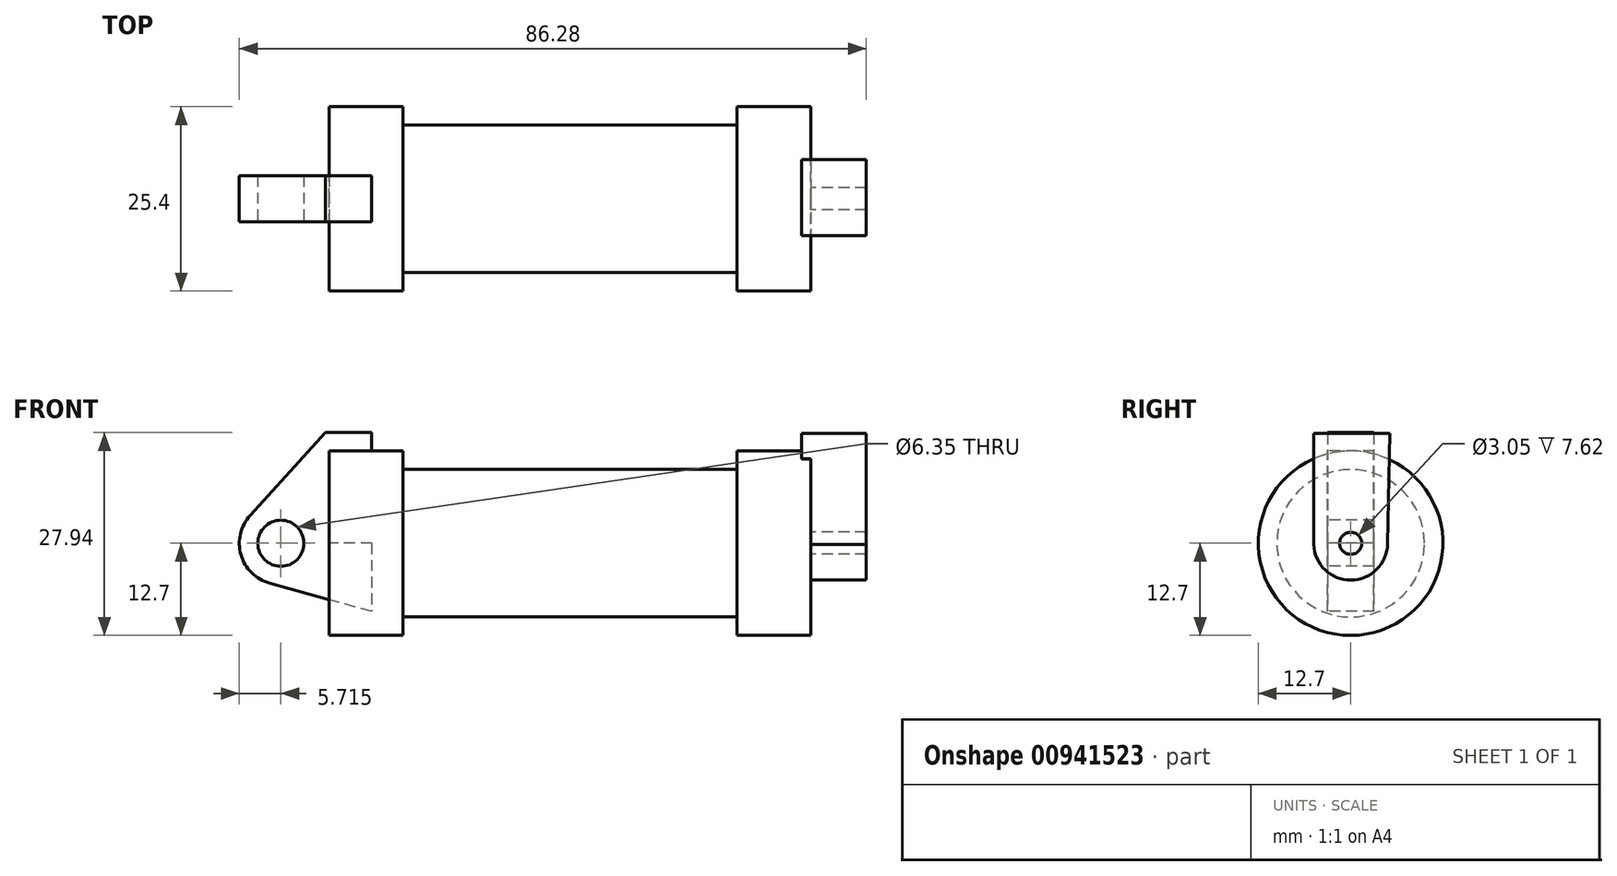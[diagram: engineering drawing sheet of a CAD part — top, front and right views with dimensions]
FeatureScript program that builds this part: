
annotation { "Feature Type Name" : "Feature", "Feature Type Description" : "" }
export const myFeature = defineFeature(function(context is Context, id is Id, definition is map)
    precondition{}
    {
        {
            var Q0;
            Q0=qCreatedBy(makeId("Front.planeOp"),FACE);
            var sketch = newSketch(context, id + "F0", { "sketchPlane" : qUnion([Q0])});
            skLineSegment(sketch, "E0", {"start": v(0, 0) * mm, "end": v(0, 12.7) * mm});
            skLineSegment(sketch, "E1", {"start": v(0, 12.7) * mm, "end": v(10.16, 12.7) * mm});
            skLineSegment(sketch, "E2", {"start": v(10.16, 12.7) * mm, "end": v(10.16, 10.16) * mm});
            skLineSegment(sketch, "E3", {"start": v(10.16, 10.16) * mm, "end": v(56.13, 10.16) * mm});
            skLineSegment(sketch, "E4", {"start": v(56.13, 10.16) * mm, "end": v(56.13, 12.7) * mm});
            skLineSegment(sketch, "E5", {"start": v(56.13, 12.7) * mm, "end": v(66.3, 12.7) * mm});
            skLineSegment(sketch, "E6", {"start": v(66.3, 12.7) * mm, "end": v(66.3, 0) * mm});
            skLineSegment(sketch, "E7", {"start": v(66.3, 0) * mm, "end": v(0, 0) * mm});
            skLineSegment(sketch, "E8", {"start": v(5.84, 15.24) * mm, "end": v(-0.5, 15.24) * mm});
            skLineSegment(sketch, "E9", {"start": v(-0.5, 15.24) * mm, "end": v(-10.88, 3.85) * mm});
            skLineSegment(sketch, "E10", {"start": v(0, 0) * mm, "end": v(-6.65, 0) * mm});
            skCircle(sketch, "E11", {"center": v(-6.65, 0) * mm, "radius": 5.72 * mm});
            skCircle(sketch, "E12", {"center": v(-6.65, 0) * mm, "radius": 3.18 * mm});
            skLineSegment(sketch, "E13", {"start": v(5.84, 15.24) * mm, "end": v(5.84, -9.4) * mm});
            skLineSegment(sketch, "E14", {"start": v(5.84, -9.4) * mm, "end": v(-8.18, -5.5) * mm});
            skSolve(sketch);
        }
        {
            var Q0;
            {var subQ0=sQuery(id+"F0.wireOp",EDGE,"E0");Q0=makeQuery(id+"F0.imprint","IMPRINT",FACE,{"disambiguationData":[TD([[makeQuery(id+"F0.imprint","IMPRINT",EDGE,{"derivedFrom":subQ0}),-1.0]])]});}
            var Q1;
            {var subQ0=sQuery(id+"F0.wireOp",EDGE,"E2");Q1=makeQuery(id+"F0.imprint","IMPRINT",FACE,{"disambiguationData":[TD([[makeQuery(id+"F0.imprint","IMPRINT",EDGE,{"derivedFrom":subQ0}),-1.0]])]});}
            var Q2;
            Q2=sQuery(id+"F0.wireOp",EDGE,"E7");
            revolve(context, id + "F1", {"surfaceOperationType" : NewSurfaceOperationType.NEW, "entities" : qUnion([Q0, Q1]), "axis" : qUnion([Q2]), "revolveType" : RevolveType.FULL});
        }
        {
            var Q0;
            {var subQ1=sQuery(id+"F0.wireOp",EDGE,"E0");Q0=makeQuery(id+"F0.imprint","IMPRINT",FACE,{"disambiguationData":[TD([[makeQuery(id+"F0.imprint","IMPRINT",EDGE,{"derivedFrom":subQ1}),1.0]])]});}
            var Q1;
            {var subQ5=sQuery(id+"F0.wireOp",EDGE,"E12");Q1=makeQuery(id+"F0.imprint","IMPRINT",FACE,{"disambiguationData":[TD([[makeQuery(id+"F0.imprint","IMPRINT",EDGE,{"derivedFrom":subQ5}),-1.0]])]});}
            var Q2;
            {var subQ0=sQuery(id+"F0.wireOp",EDGE,"E14");Q2=makeQuery(id+"F0.imprint","IMPRINT",FACE,{"disambiguationData":[TD([[makeQuery(id+"F0.imprint","IMPRINT",EDGE,{"derivedFrom":subQ0}),-1.0]])]});}
            extrude(context, id + "F2", {"entities" : qUnion([Q0, Q1, Q2]), "oppositeDirection" : true, "depth" : 6.35 * mm, "offsetDistance" : 25.4 * mm, "symmetric" : true});
        }
        {
            var Q0;
            Q0=makeQuery(id+"F1.opRevolve","SWEPT_FACE",FACE,{"disambiguationData":[OSD([sQuery(id+"F0.wireOp",EDGE,"E6")])]});
            var sketch = newSketch(context, id + "F3", { "sketchPlane" : qUnion([Q0])});
            skCircle(sketch, "E15", {"center": v(0, 0) * mm, "radius": 5.08 * mm});
            skCircle(sketch, "E16", {"center": v(0, 0) * mm, "radius": 1.52 * mm});
            skLineSegment(sketch, "E17", {"start": v(-5.08, -0.17) * mm, "end": v(-5.08, 15.13) * mm});
            skLineSegment(sketch, "E18", {"start": v(-5.08, 15.13) * mm, "end": v(5.4, 15.13) * mm});
            skLineSegment(sketch, "E19", {"start": v(5.4, 15.13) * mm, "end": v(5.08, -0.1) * mm});
            skSolve(sketch);
        }
        {
            var Q0;
            {var subQ0=sQuery(id+"F3.wireOp",EDGE,"E19");var subQ1=sQuery(id+"F3.wireOp",EDGE,"E15");var subQ2=makeQuery(id+"F3.imprint","INTERSECT",VERTEX,{"derivedFrom":[subQ1,subQ0]});Q0=makeQuery(id+"F3.imprint","IMPRINT",FACE,{"disambiguationData":[TD([[makeQuery(id+"F3.imprint","IMPRINT",EDGE,{"disambiguationData":[TD([[subQ2,-1.0]])],"derivedFrom":subQ1}),-1.0]])]});}
            var Q1;
            Q1=makeQuery(id+"F3.imprint","IMPRINT",FACE,{"disambiguationData":[TD([[makeQuery(id+"F3.imprint","IMPRINT",EDGE,{"derivedFrom":sQuery(id+"F3.wireOp",EDGE,"E16")}),-1.0]])]});
            var Q2;
            {var subQ0=sQuery(id+"F3.wireOp",EDGE,"E18");Q2=makeQuery(id+"F3.imprint","IMPRINT",FACE,{"disambiguationData":[TD([[makeQuery(id+"F3.imprint","IMPRINT",EDGE,{"derivedFrom":subQ0}),-1.0]])]});}
            extrude(context, id + "F4", {"entities" : qUnion([Q0, Q1, Q2]), "operationType" : NewBodyOperationType.ADD, "depth" : 7.62 * mm, "offsetDistance" : 25.4 * mm, "hasSecondDirection" : true, "secondDirectionOppositeDirection" : true, "secondDirectionDepth" : 1.27 * mm});
        }
    });
